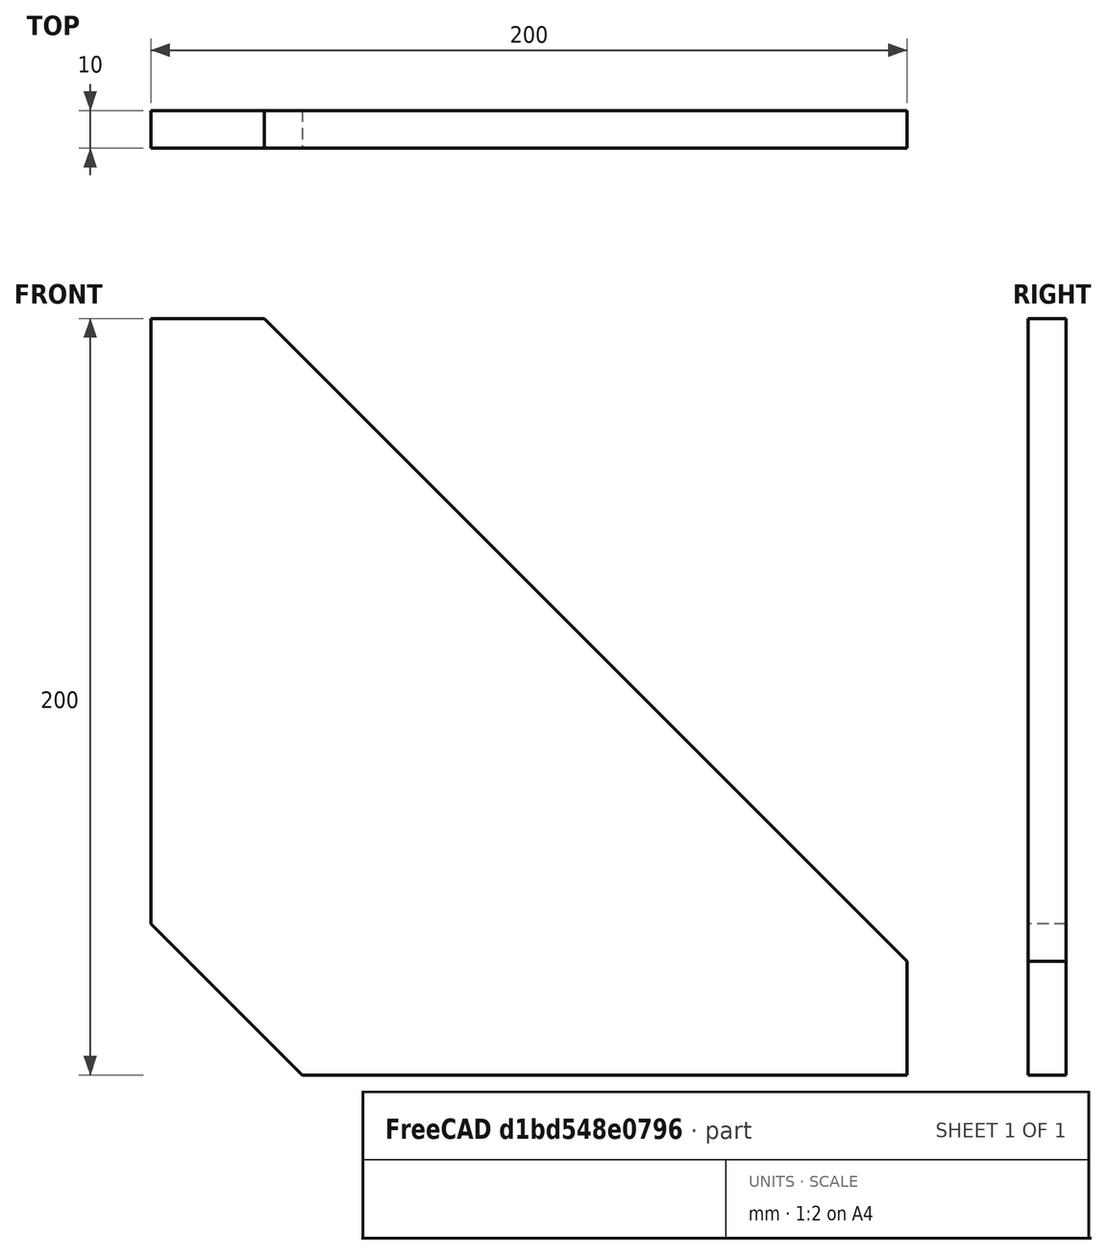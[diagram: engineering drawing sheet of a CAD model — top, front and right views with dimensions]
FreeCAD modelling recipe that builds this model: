
FCSTD DOCUMENT  (FreeCAD 0.21R30492 (Git))
Label: がセットプレート
License: All rights reserved
LicenseURL: http://en.wikipedia.org/wiki/All_rights_reserved
objects: Sketcher::SketchObject×1, PartDesign::Pad×1, PartDesign::Body×1
note: 4 computed .brp shape members not serialized (recipe doc carries the construction recipe); baked Part::Feature solids carry a one-line shape summary decoded from their .brp

FEATURE [Sketcher::SketchObject] Sketch
  FullyConstrained = true
  MapMode = 5
  Placement = pos=(0,0,0) rot=(1,0,0;1.5708rad)
  Support = -> [XZ_Plane]
  sketch-geometry (6):
    g0: LineSegment StartX=40 StartY=0 StartZ=0 EndX=200 EndY=0 EndZ=0
    g1: LineSegment StartX=200 StartY=0 StartZ=0 EndX=200 EndY=30 EndZ=0
    g2: LineSegment StartX=30 StartY=200 StartZ=0 EndX=0 EndY=200 EndZ=0
    g3: LineSegment StartX=0 StartY=200 StartZ=0 EndX=0 EndY=40 EndZ=0
    g4: LineSegment StartX=30 StartY=200 StartZ=0 EndX=200 EndY=30 EndZ=0
    g5: LineSegment StartX=40 StartY=0 StartZ=0 EndX=0 EndY=40 EndZ=0
  constraints (18):
    c: Coincident(g0,g1)
    c: Coincident(g2,g3)
    c: Horizontal(g0)
    c: Horizontal(g2)
    c: Vertical(g1)
    c: Vertical(g3)
    c: Coincident(g2,g4)
    c: Coincident(g1,g4)
    c: Coincident(g0,g5)
    c: Coincident(g3,g5)
    c: DistanceY(g-1,g2) = 200  'H'
    c: DistanceX(g-1,g0) = 200  'W'
    c: DistanceX(g3,g0) = 40  'c'
    c: PointOnObject(g3,g-2)
    c: DistanceY(g1,g1) = 30  'b'
    c: DistanceX(g2,g2) = 30  'a'
    c: PointOnObject(g0,g-1)
    c: Angle(g5,g-1) = 0.785398  'k'
FEATURE [PartDesign::Pad] Pad
  Direction = (0,-1,-2e-16)
  Length = 10
  Length2 = 10
  Midplane = true
  Placement = pos=(0,0,0) rot=(1,0,0;1.5708rad)
  Profile = -> Sketch
  ReferenceAxis = -> Sketch [N_Axis]
  Type = 0
FEATURE [PartDesign::Body] Body
  Group = -> [Sketch,Pad]
  Origin = -> Origin
  Tip = -> Pad
